# Revit family: WHFD-5RD-2NH
name_source: partatom
category: Plumbing Fixtures
revit_build: Autodesk Revit MEP 2016 (Build: 20150220_1215(x64)
units: mm (PartAtom-declared; Revit-internal decimal feet)

## family parameters
Cut with Voids When Loaded = No
Host = Face
OmniClass Number = 23.70.50.21.24
OmniClass Title = Waste Water Drains
Part Type = Normal
Room Calculation Point = No
Round Connector Dimension = Use Diameter
Shared = Yes

## types (1)
- WHFD-5RD-2NH
    Amperage = 0
    CW Connection = No
    Default Elevation = 0"
    Description = WHFD-5RD-2NH - Ligature Resistant 5" Round floor Drain, Strainer and Grate
    HW Connection = No
    Manufacturer = Whitehall
    Material = Type 304 Stainless Steel
    Model = WHFD-5RD-2NH
    Revised Date = 10/04/19
    Tempered Water Connection = No
    URL = http://www.whitehallmfg.com
    Vent Connection = No
    Voltage = 0
    WHFD-5RD-2NH - Ligature Resistant 5" Round floor Drain, Strainer and Grate = Yes
    Waste Connection = Yes

## geometry (parser evidence)
native form markers: Sweep x1
no freeform markers — native parametric forms only
